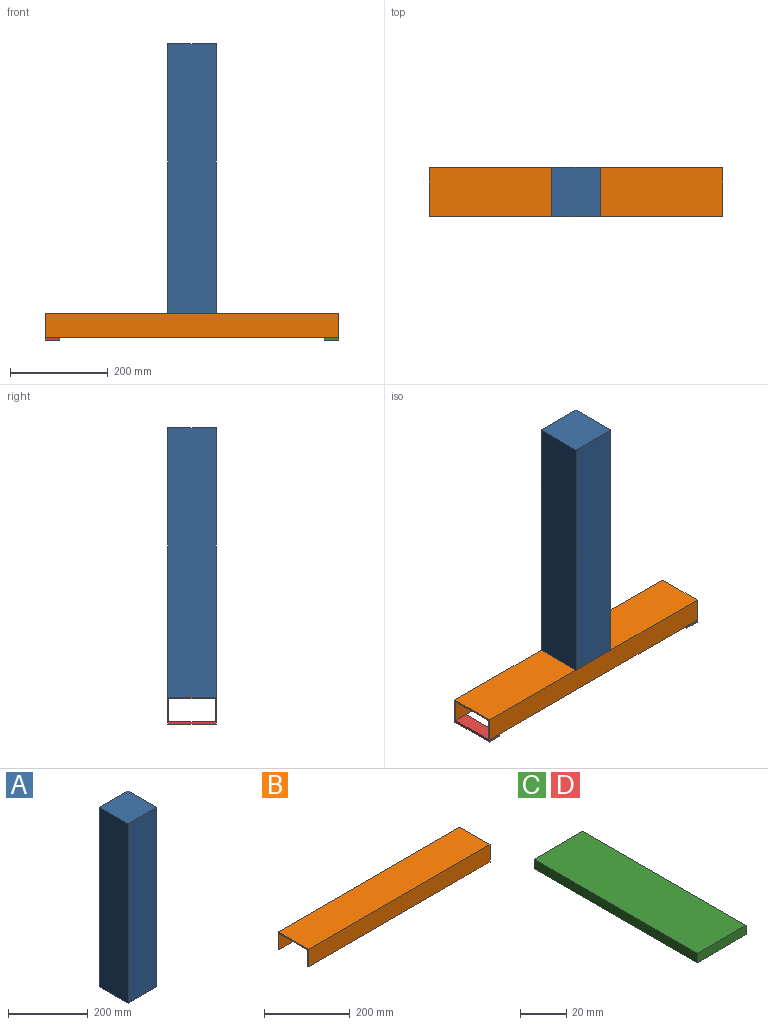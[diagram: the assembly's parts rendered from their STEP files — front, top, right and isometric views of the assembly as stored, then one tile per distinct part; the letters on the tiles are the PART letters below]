
ASSEMBLY  parts=4 mates=3
PART A: 6 faces, bbox 100x100x550 mm
  f0: plane 550x100mm, normal (0,-1,0), area 55000mm2, adj f1,f3,f4,f5
  f1: plane 550x100mm, normal (1,0,0), area 55000mm2, adj f0,f2,f4,f5
  f2: plane 550x100mm, normal (0,1,0), area 55000mm2, adj f1,f3,f4,f5
  f3: plane 550x100mm, normal (-1,0,0), area 55000mm2, adj f0,f2,f4,f5
  f4: plane 100x100mm, normal (0,0,-1), area 10000mm2, adj f0,f1,f2,f3
  f5: plane 100x100mm, normal (0,0,1), area 10000mm2, adj f0,f1,f2,f3
PART B: 10 faces, bbox 600x100x50 mm
  f0: plane 600x100mm, normal (0,0,1), area 60000mm2, adj f1,f7,f8,f9
  f1: plane 600x50mm, normal (0,-1,0), area 30000mm2, adj f0,f2,f8,f9
  f2: plane 600x3mm, normal (0,0,-1), area 1800mm2, adj f1,f3,f8,f9
  f3: plane 600x47mm, normal (0,1,0), area 28200mm2, adj f2,f4,f8,f9
  f4: plane 600x94mm, normal (0,0,-1), area 56400mm2, adj f3,f5,f8,f9
  f5: plane 600x47mm, normal (0,-1,0), area 28200mm2, adj f4,f6,f8,f9
  f6: plane 600x3mm, normal (0,0,-1), area 1800mm2, adj f5,f7,f8,f9
  f7: plane 600x50mm, normal (0,1,0), area 30000mm2, adj f0,f6,f8,f9
  f8: plane 100x50mm, normal (-1,0,0), area 582mm2, adj f0,f1,f2,f3,f4,f5,f6,f7
  f9: plane 100x50mm, normal (1,0,0), area 582mm2, adj f0,f1,f2,f3,f4,f5,f6,f7
PART C: 6 faces, bbox 30x100x5 mm
  f0: plane 30x5mm, normal (0,-1,0), area 150mm2, adj f1,f3,f4,f5
  f1: plane 100x5mm, normal (1,0,0), area 500mm2, adj f0,f2,f4,f5
  f2: plane 30x5mm, normal (0,1,0), area 150mm2, adj f1,f3,f4,f5
  f3: plane 100x5mm, normal (-1,0,0), area 500mm2, adj f0,f2,f4,f5
  f4: plane 100x30mm, normal (0,0,1), area 3000mm2, adj f0,f1,f2,f3
  f5: plane 100x30mm, normal (0,0,-1), area 3000mm2, adj f0,f1,f2,f3
PART D: same geometry as C
PLACE A at identity fixed
PLACE B t=(0,0,-550)mm
PLACE C rot(axis=(0,0,-1),180deg) t=(285,0,-605)mm
PLACE D rot(axis=(0,0,-1),180deg) t=(-285,0,-605)mm
MATE fastened D.f2 <-> B.f1  axis (0,-1,0) through (-300,-50,-600)mm
MATE fastened C.f0 <-> B.f7  axis (0,-1,0) through (300,50,-600)mm
MATE fastened B.f0 <-> A.f4  axis (0,0,1) through (0,0,-550)mm
